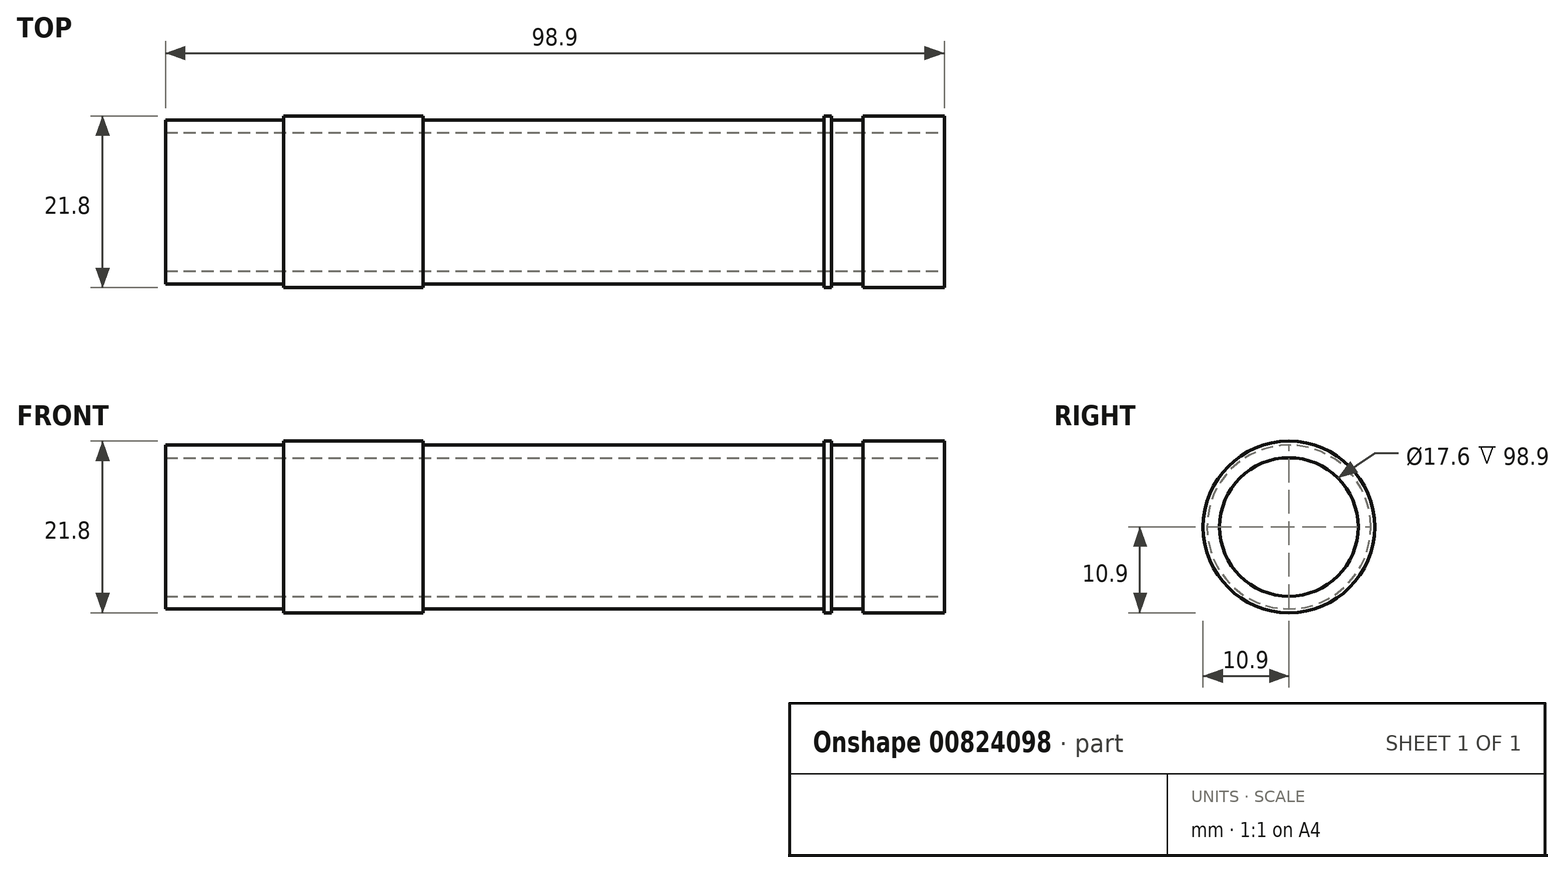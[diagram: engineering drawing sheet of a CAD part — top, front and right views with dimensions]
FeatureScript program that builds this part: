
annotation { "Feature Type Name" : "Feature", "Feature Type Description" : "" }
export const myFeature = defineFeature(function(context is Context, id is Id, definition is map)
    precondition{}
    {
        {
            var Q0;
            Q0=qCreatedBy(makeId("Right.planeOp"),FACE);
            var sketch = newSketch(context, id + "F0", { "sketchPlane" : qUnion([Q0])});
            skCircle(sketch, "E0", {"center": v(0, 0) * mm, "radius": 8.8 * mm});
            skCircle(sketch, "E1", {"center": v(0, 0) * mm, "radius": 10.4 * mm});
            skSolve(sketch);
        }
        {
            var Q0;
            Q0=makeQuery(id+"F0.imprint","IMPRINT",FACE,{"disambiguationData":[TD([[makeQuery(id+"F0.imprint","IMPRINT",EDGE,{"derivedFrom":sQuery(id+"F0.wireOp",EDGE,"E0")}),1.0]])]});
            var Q1;
            Q1=makeQuery(id+"F0.imprint","IMPRINT",FACE,{"disambiguationData":[TD([[makeQuery(id+"F0.imprint","IMPRINT",EDGE,{"derivedFrom":sQuery(id+"F0.wireOp",EDGE,"E0")}),-1.0]])]});
            extrude(context, id + "F1", {"entities" : qUnion([Q0, Q1]), "oppositeDirection" : true, "depth" : 13.1 * mm, "offsetDistance" : 25 * mm});
        }
        {
            var Q0;
            Q0=makeQuery(id+"F0.imprint","IMPRINT",FACE,{"disambiguationData":[TD([[makeQuery(id+"F0.imprint","IMPRINT",EDGE,{"derivedFrom":sQuery(id+"F0.wireOp",EDGE,"E0")}),1.0]])]});
            extrude(context, id + "F2", {"entities" : qUnion([Q0]), "operationType" : NewBodyOperationType.REMOVE, "oppositeDirection" : true, "depth" : 25 * mm, "offsetDistance" : 25 * mm});
        }
        {
            var Q0;
            Q0=makeQuery(id+"F1.opExtrude","CAP_FACE",FACE,{"disambiguationData":[OSD([sQuery(id+"F0.wireOp",EDGE,"E1")])],"isStart":false});
            extrude(context, id + "F3", {"entities" : qUnion([Q0]), "operationType" : NewBodyOperationType.ADD, "depth" : 1.9 * mm, "offsetDistance" : 25 * mm});
        }
        {
            var Q0;
            Q0=makeQuery(id+"F0.imprint","IMPRINT",FACE,{"disambiguationData":[TD([[makeQuery(id+"F0.imprint","IMPRINT",EDGE,{"derivedFrom":sQuery(id+"F0.wireOp",EDGE,"E0")}),-1.0]])]});
            var sketch = newSketch(context, id + "F4", { "sketchPlane" : qUnion([Q0])});
            skCircle(sketch, "E2", {"center": v(0, 0) * mm, "radius": 10.9 * mm});
            skSolve(sketch);
        }
        {
            var Q0;
            Q0=makeQuery(id+"F4.imprint","IMPRINT",FACE,{"disambiguationData":[TD([[makeQuery(id+"F4.imprint","IMPRINT",EDGE,{"derivedFrom":sQuery(id+"F4.wireOp",EDGE,"E2")}),1.0]])]});
            var Q1;
            Q1=makeQuery(id+"F0.imprint","IMPRINT",FACE,{"disambiguationData":[TD([[makeQuery(id+"F0.imprint","IMPRINT",EDGE,{"derivedFrom":sQuery(id+"F0.wireOp",EDGE,"E0")}),-1.0]])]});
            extrude(context, id + "F5", {"entities" : qUnion([Q0, Q1]), "operationType" : NewBodyOperationType.ADD, "depth" : 17.7 * mm, "offsetDistance" : 25 * mm});
        }
        {
            var Q0;
            Q0=makeQuery(id+"F0.imprint","IMPRINT",FACE,{"disambiguationData":[TD([[makeQuery(id+"F0.imprint","IMPRINT",EDGE,{"derivedFrom":sQuery(id+"F0.wireOp",EDGE,"E0")}),-1.0]])]});
            extrude(context, id + "F6", {"entities" : qUnion([Q0]), "operationType" : NewBodyOperationType.ADD, "depth" : 68.6 * mm, "offsetDistance" : 25 * mm});
        }
        {
            var Q0;
            Q0=makeQuery(id+"F6.opExtrude","CAP_FACE",FACE,{"disambiguationData":[OSD([sQuery(id+"F0.wireOp",EDGE,"E0"),sQuery(id+"F0.wireOp",EDGE,"E1")])],"isStart":false});
            var sketch = newSketch(context, id + "F7", { "sketchPlane" : qUnion([Q0])});
            skCircle(sketch, "E3", {"center": v(0, 0) * mm, "radius": 10.9 * mm});
            skSolve(sketch);
        }
        {
            var Q0;
            Q0=makeQuery(id+"F7.imprint","IMPRINT",FACE,{"disambiguationData":[TD([[makeQuery(id+"F7.imprint","IMPRINT",EDGE,{"derivedFrom":sQuery(id+"F7.wireOp",EDGE,"E3")}),1.0]])]});
            var Q1;
            Q1=makeQuery(id+"F7.imprint","IMPRINT",FACE,{"disambiguationData":[TD([[makeQuery(id+"F7.imprint","IMPRINT",EDGE,{"derivedFrom":makeQuery(id+"F6.opExtrude","CAP_EDGE",EDGE,{"disambiguationData":[OSD([sQuery(id+"F0.wireOp",EDGE,"E0")])],"isStart":false})}),-1.0]])]});
            extrude(context, id + "F8", {"entities" : qUnion([Q0, Q1]), "operationType" : NewBodyOperationType.ADD, "depth" : 1 * mm, "offsetDistance" : 25 * mm});
        }
        {
            var Q0;
            Q0=makeQuery(id+"F8.opExtrude","CAP_FACE",FACE,{"disambiguationData":[OSD([sQuery(id+"F0.wireOp",EDGE,"E0"),sQuery(id+"F7.wireOp",EDGE,"E3")])],"isStart":false});
            var sketch = newSketch(context, id + "F9", { "sketchPlane" : qUnion([Q0])});
            skCircle(sketch, "E4", {"center": v(0, 0) * mm, "radius": 10.4 * mm});
            skSolve(sketch);
        }
        {
            var Q0;
            Q0=makeQuery(id+"F9.imprint","IMPRINT",FACE,{"disambiguationData":[TD([[makeQuery(id+"F9.imprint","IMPRINT",EDGE,{"derivedFrom":sQuery(id+"F9.wireOp",EDGE,"E4")}),1.0]])]});
            extrude(context, id + "F10", {"entities" : qUnion([Q0]), "operationType" : NewBodyOperationType.ADD, "depth" : 4 * mm, "offsetDistance" : 25 * mm});
        }
        {
            var Q0;
            Q0=makeQuery(id+"F10.opExtrude","CAP_FACE",FACE,{"disambiguationData":[OSD([sQuery(id+"F0.wireOp",EDGE,"E0"),sQuery(id+"F9.wireOp",EDGE,"E4")])],"isStart":false});
            var sketch = newSketch(context, id + "F11", { "sketchPlane" : qUnion([Q0])});
            skCircle(sketch, "E5", {"center": v(0, 0) * mm, "radius": 10.9 * mm});
            skSolve(sketch);
        }
        {
            var Q0;
            Q0=makeQuery(id+"F11.imprint","IMPRINT",FACE,{"disambiguationData":[TD([[makeQuery(id+"F11.imprint","IMPRINT",EDGE,{"derivedFrom":makeQuery(id+"F10.opExtrude","CAP_EDGE",EDGE,{"disambiguationData":[OSD([sQuery(id+"F9.wireOp",EDGE,"E4")])],"isStart":false})}),1.0]])]});
            var Q1;
            Q1=makeQuery(id+"F11.imprint","IMPRINT",FACE,{"disambiguationData":[TD([[makeQuery(id+"F11.imprint","IMPRINT",EDGE,{"derivedFrom":sQuery(id+"F11.wireOp",EDGE,"E5")}),1.0]])]});
            extrude(context, id + "F12", {"entities" : qUnion([Q0, Q1]), "operationType" : NewBodyOperationType.ADD, "depth" : 10.3 * mm, "offsetDistance" : 25 * mm});
        }
    });
